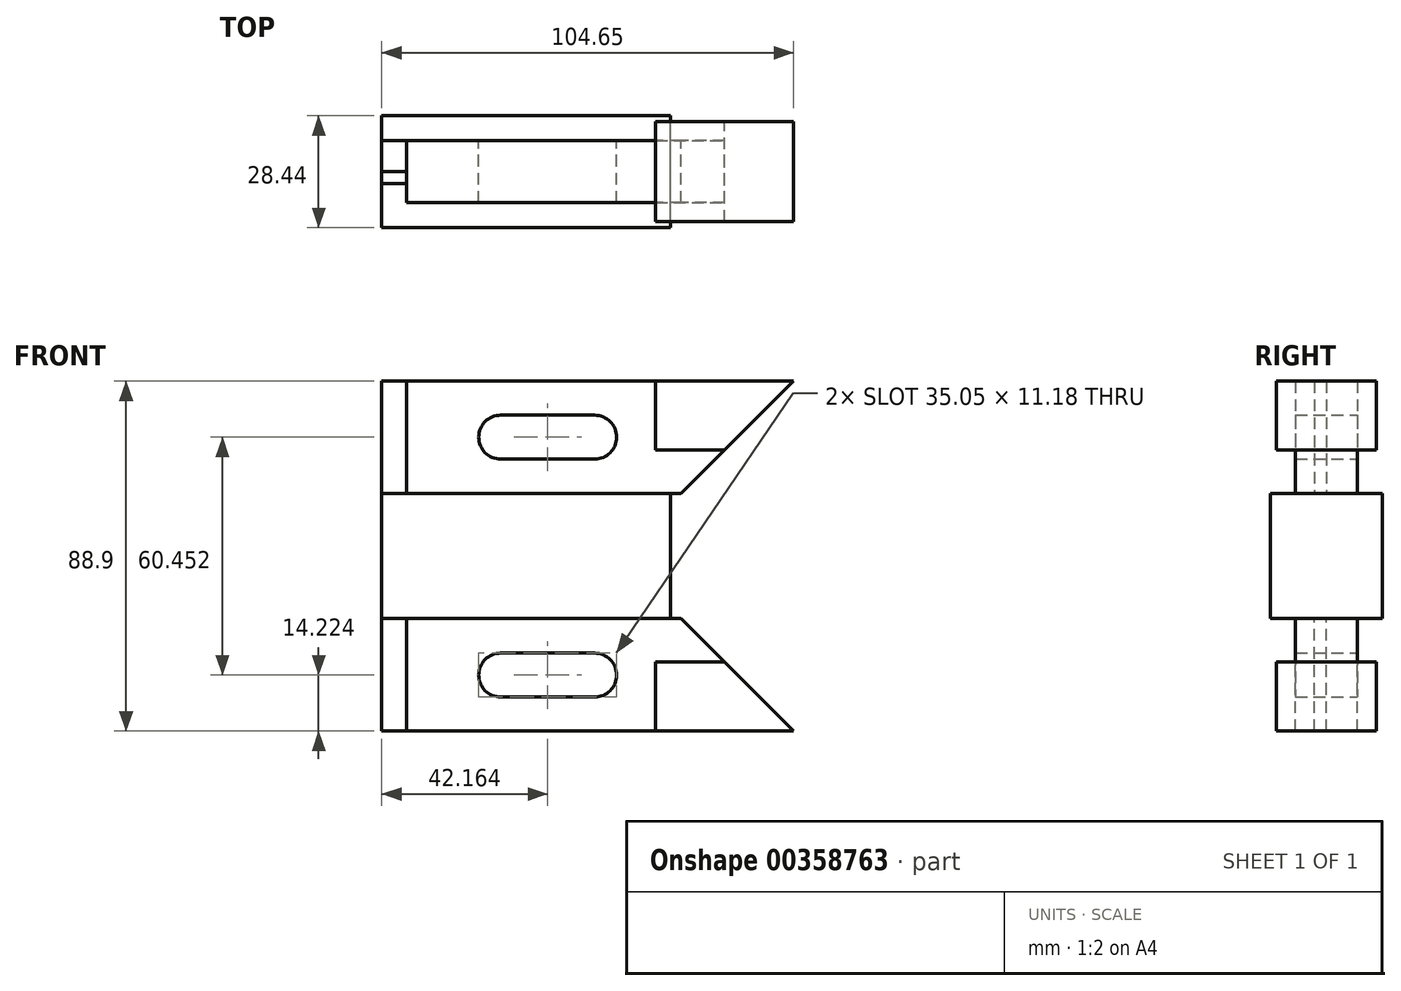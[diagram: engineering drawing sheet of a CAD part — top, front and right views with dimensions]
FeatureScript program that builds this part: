
annotation { "Feature Type Name" : "Feature", "Feature Type Description" : "" }
export const myFeature = defineFeature(function(context is Context, id is Id, definition is map)
    precondition{}
    {
        {
            var Q0;
            Q0=qCreatedBy(makeId("Front.planeOp"),FACE);
            var sketch = newSketch(context, id + "F0", { "sketchPlane" : qUnion([Q0])});
            skLineSegment(sketch, "E0", {"start": v(0, 44.45) * mm, "end": v(0, 0) * mm});
            skLineSegment(sketch, "E1", {"start": v(-72.54, 0) * mm, "end": v(89.26, 0) * mm, "construction": true});
            skLineSegment(sketch, "E2", {"start": v(0, 44.45) * mm, "end": v(104.65, 44.45) * mm});
            skLineSegment(sketch, "E3", {"start": v(69.6, 44.45) * mm, "end": v(69.6, 26.92) * mm});
            skLineSegment(sketch, "E4", {"start": v(69.6, 26.92) * mm, "end": v(87.12, 26.92) * mm});
            skLineSegment(sketch, "E5", {"start": v(6.35, 44.45) * mm, "end": v(6.35, 15.88) * mm});
            skLineSegment(sketch, "E6", {"start": v(30.23, 30.23) * mm, "end": v(54.1, 30.23) * mm, "construction": true});
            skLineSegment(sketch, "E7", {"start": v(104.65, 44.45) * mm, "end": v(87.12, 26.92) * mm});
            skLineSegment(sketch, "E8", {"start": v(87.12, 26.92) * mm, "end": v(76.07, 15.88) * mm});
            skLineSegment(sketch, "E9", {"start": v(76.07, 15.88) * mm, "end": v(6.35, 15.88) * mm});
            skLineSegment(sketch, "E10", {"start": v(6.35, 15.88) * mm, "end": v(0, 15.88) * mm});
            skLineSegment(sketch, "E11", {"start": v(73.4, 15.88) * mm, "end": v(73.4, 0) * mm});
            skArc(sketch, "E12.0.startCap", {"start": v(30.23, 24.64) * mm, "mid": v(24.64, 30.23) * mm, "end": v(30.23, 35.81) * mm});
            skArc(sketch, "E12.0.endCap", {"start": v(54.1, 35.81) * mm, "mid": v(59.7, 30.23) * mm, "end": v(54.1, 24.64) * mm});
            skLineSegment(sketch, "E12.0.left", {"start": v(30.23, 35.81) * mm, "end": v(54.1, 35.81) * mm});
            skLineSegment(sketch, "E12.0.right", {"start": v(30.23, 24.64) * mm, "end": v(54.1, 24.64) * mm});
            skPoint(sketch, "E13", {"position": v(24.64, 30.23) * mm});
            skPoint(sketch, "E14", {"position": v(59.7, 30.23) * mm});
            skArc(sketch, "E15.MirrorCS", {"start": v(30.23, -24.64) * mm, "mid": v(24.64, -30.23) * mm, "end": v(30.23, -35.81) * mm});
            skPoint(sketch, "E16.MirrorP", {"position": v(24.64, -30.23) * mm});
            skLineSegment(sketch, "E17.MirrorCS", {"start": v(73.4, -15.88) * mm, "end": v(73.4, 0) * mm});
            skLineSegment(sketch, "E18.MirrorCS", {"start": v(6.35, -15.88) * mm, "end": v(0, -15.88) * mm});
            skPoint(sketch, "E19.MirrorP", {"position": v(59.7, -30.23) * mm});
            skLineSegment(sketch, "E20.MirrorCS", {"start": v(76.07, -15.88) * mm, "end": v(6.35, -15.88) * mm});
            skLineSegment(sketch, "E21.MirrorCS", {"start": v(87.12, -26.92) * mm, "end": v(76.07, -15.88) * mm});
            skLineSegment(sketch, "E22.MirrorCS", {"start": v(30.23, -24.64) * mm, "end": v(54.1, -24.64) * mm});
            skLineSegment(sketch, "E23.MirrorCS", {"start": v(30.23, -35.81) * mm, "end": v(54.1, -35.81) * mm});
            skLineSegment(sketch, "E24.MirrorCS", {"start": v(104.65, -44.45) * mm, "end": v(87.12, -26.92) * mm});
            skLineSegment(sketch, "E25.MirrorCS", {"start": v(6.35, -44.45) * mm, "end": v(6.35, -15.88) * mm});
            skLineSegment(sketch, "E26.MirrorCS", {"start": v(0, -44.45) * mm, "end": v(0, 0) * mm});
            skArc(sketch, "E27.MirrorCS", {"start": v(54.1, -35.81) * mm, "mid": v(59.7, -30.23) * mm, "end": v(54.1, -24.64) * mm});
            skLineSegment(sketch, "E28.MirrorCS", {"start": v(69.6, -26.92) * mm, "end": v(87.12, -26.92) * mm});
            skLineSegment(sketch, "E29.MirrorCS", {"start": v(0, -44.45) * mm, "end": v(104.65, -44.45) * mm});
            skLineSegment(sketch, "E30.MirrorCS", {"start": v(69.6, -44.45) * mm, "end": v(69.6, -26.92) * mm});
            skSolve(sketch);
        }
        {
            var Q0;
            {var subQ1=sQuery(id+"F0.wireOp",EDGE,"E10");Q0=makeQuery(id+"F0.imprint","IMPRINT",FACE,{"disambiguationData":[TD([[makeQuery(id+"F0.imprint","IMPRINT",EDGE,{"derivedFrom":subQ1}),1.0]])]});}
            extrude(context, id + "F1", {"entities" : qUnion([Q0]), "endBound" : BoundingType.SYMMETRIC, "depth" : 28.45 * mm});
        }
        {
            var Q0;
            {var subQ0=sQuery(id+"F0.wireOp",EDGE,"E24.MirrorCS");Q0=makeQuery(id+"F0.imprint","IMPRINT",FACE,{"disambiguationData":[TD([[makeQuery(id+"F0.imprint","IMPRINT",EDGE,{"derivedFrom":subQ0}),1.0]])]});}
            var Q1;
            {var subQ2=sQuery(id+"F0.wireOp",EDGE,"E3");Q1=makeQuery(id+"F0.imprint","IMPRINT",FACE,{"disambiguationData":[TD([[makeQuery(id+"F0.imprint","IMPRINT",EDGE,{"derivedFrom":subQ2}),1.0]])]});}
            extrude(context, id + "F2", {"entities" : qUnion([Q0, Q1]), "endBound" : BoundingType.SYMMETRIC, "depth" : 25.4 * mm});
        }
        {
            var Q0;
            {var subQ4=sQuery(id+"F0.wireOp",EDGE,"E3");Q0=makeQuery(id+"F0.imprint","IMPRINT",FACE,{"disambiguationData":[TD([[makeQuery(id+"F0.imprint","IMPRINT",EDGE,{"derivedFrom":subQ4}),-1.0]])]});}
            var Q1;
            Q1=makeQuery(id+"F0.imprint","IMPRINT",FACE,{"disambiguationData":[TD([[makeQuery(id+"F0.imprint","IMPRINT",EDGE,{"derivedFrom":sQuery(id+"F0.wireOp",EDGE,"E15.MirrorCS")}),-1.0]])]});
            extrude(context, id + "F3", {"entities" : qUnion([Q0, Q1]), "endBound" : BoundingType.SYMMETRIC, "depth" : 15.75 * mm});
        }
        {
            var Q0;
            {var subQ4=sQuery(id+"F0.wireOp",EDGE,"E5");Q0=makeQuery(id+"F0.imprint","IMPRINT",FACE,{"disambiguationData":[TD([[makeQuery(id+"F0.imprint","IMPRINT",EDGE,{"derivedFrom":subQ4}),-1.0]])]});}
            var Q1;
            {var subQ0=sQuery(id+"F0.wireOp",EDGE,"E18.MirrorCS");Q1=makeQuery(id+"F0.imprint","IMPRINT",FACE,{"disambiguationData":[TD([[makeQuery(id+"F0.imprint","IMPRINT",EDGE,{"derivedFrom":subQ0}),1.0]])]});}
            extrude(context, id + "F4", {"entities" : qUnion([Q0, Q1]), "depth" : 3.05 * mm});
        }
        {
            var Q0;
            {var subQ0=sQuery(id+"F0.wireOp",EDGE,"E18.MirrorCS");Q0=makeQuery(id+"F0.imprint","IMPRINT",FACE,{"disambiguationData":[TD([[makeQuery(id+"F0.imprint","IMPRINT",EDGE,{"derivedFrom":subQ0}),1.0]])]});}
            var Q1;
            {var subQ4=sQuery(id+"F0.wireOp",EDGE,"E5");Q1=makeQuery(id+"F0.imprint","IMPRINT",FACE,{"disambiguationData":[TD([[makeQuery(id+"F0.imprint","IMPRINT",EDGE,{"derivedFrom":subQ4}),-1.0]])]});}
            extrude(context, id + "F5", {"entities" : qUnion([Q0, Q1]), "oppositeDirection" : true, "depth" : 7.87 * mm});
        }
    });
